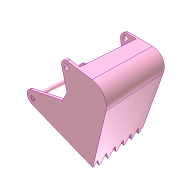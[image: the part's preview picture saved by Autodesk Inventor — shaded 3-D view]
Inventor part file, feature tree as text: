
AUTODESK INVENTOR PART (.ipt)
format: ipt  version: unknown  size: 334,336 bytes
history: native  units: in
note: dims shown in document units (in); Inventor stores cm internally (conversion verified against a paired STEP export)
features: extrude x5, sketch x5, fillet x2
ambient origin geometry x8: Origin, YZ Plane, XZ Plane, XY Plane, X Axis, Y Axis, Z Axis, Center Point
feature tree (12):
  extrude  "Extrusion43"  Depth=0.1303in
  fillet  "Fillet1"  Radius=0.0787in
  extrude  "Extrusion44"  Depth=0.7874in
  fillet  "Fillet2"  Radius=0.1575in
  extrude  "Extrusion45"  Depth=0.0984in
  extrude  "Extrusion46"  Depth=0.5841in
  extrude  "Extrusion47"  TaperAngle=15.0deg  [1 undecoded]
  sketch  "Sketch43"  dims[d200=0.0787in d201=0.1303in d202=0.0787in]
  sketch  "Sketch44"  dims[d203=0.8661in d204=0.7874in d205=0.1575in]
  sketch  "Sketch45"  dims[d206=0.0984in d207=0.0984in]
  sketch  "Sketch46"  dims[d208=15.0deg d209=0.5841in]
  sketch  "Sketch47"  dims[d210=1.1811in d211=15.0deg d213=0.7874in d214=0.4724in d215=0.7874in d216=0.9843in d217=0.0in d218=0.2362in d219=0.9055in d220=0.0in d221=0.0394in d222=0.1288in d223=0.1303in d227=0.4528in d228=0.0787in d229=0.0787in d230=0.0394in d231=0.0394in d232=0.1374in d233=0.1374in d234=1.1811in d236=0.1575in d237=0.3937in d239=0.3937in d241=0.1575in d242=0.0787in d243=0.7874in d244=0.0in d245=0.0787in d246=0.0214in d247=0.0214in d248=0.0787in d249=0.0in d250=0.0709in d251=0.9843in d252=0.0in]
note: 1 required parameter value undecoded (feature->parameter linkage not recoverable at this tier; creation-order binding heuristic only, values carry confidence <= 0.55)
